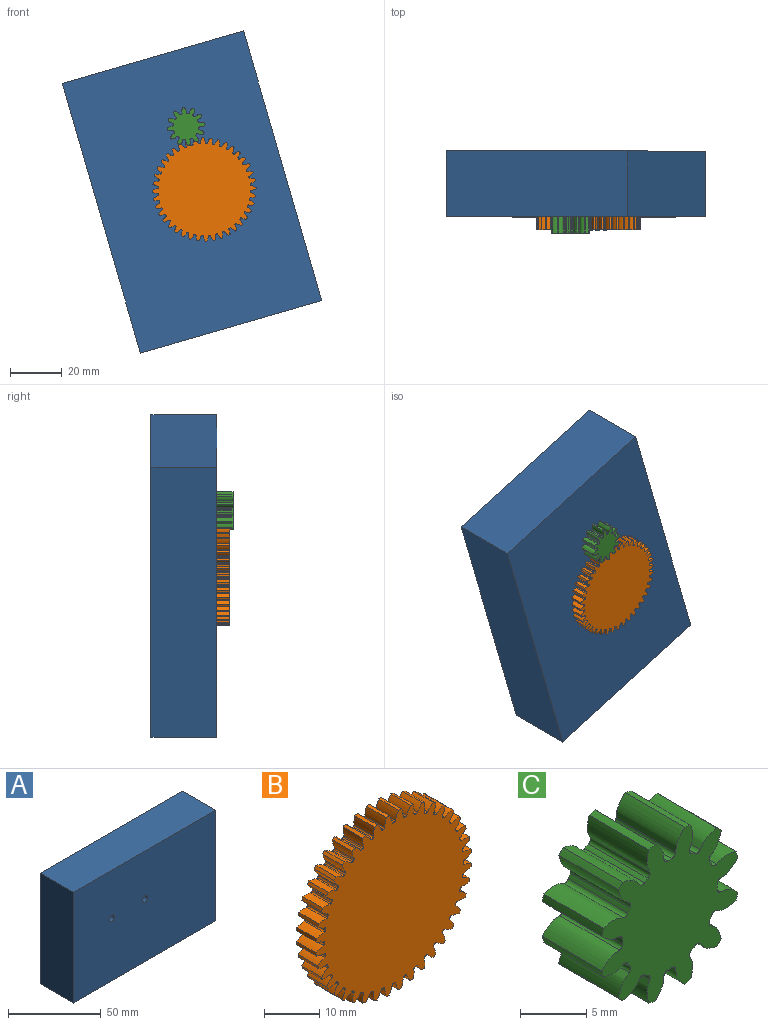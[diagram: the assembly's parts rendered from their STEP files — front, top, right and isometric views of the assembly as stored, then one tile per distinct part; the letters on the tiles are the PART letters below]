
ASSEMBLY  parts=3 mates=2
PART A: 8 faces, bbox 108.7x25.4x73 mm
  f0: plane 108.68x25.4mm, normal (0,0,1), area 2760.4mm2, adj f1,f5,f6,f7
  f1: plane 73.02x25.4mm, normal (-1,0,0), area 1854.7mm2, adj f0,f2,f6,f7
  f2: plane 108.68x25.4mm, normal (0,0,-1), area 2760.4mm2, adj f1,f5,f6,f7
  f3: cylinder r=1.91mm len=25.4mm, axis (0,-1,0), area 304mm2, adj f6,f7
  f4: cylinder r=1.91mm len=25.4mm, axis (0,-1,0), area 304mm2, adj f6,f7
  f5: plane 73.02x25.4mm, normal (1,0,0), area 1854.7mm2, adj f0,f2,f6,f7
  f6: plane 108.68x73.02mm, normal (0,1,0), area 7912.9mm2, adj f0,f1,f2,f3,f4,f5
  f7: plane 108.68x73.02mm, normal (0,-1,0), area 7912.9mm2, adj f0,f1,f2,f3,f4,f5
PART B: 242 faces, bbox 39.9x5.1x39.9 mm
  f0: extruded ~5.08x1.87mm, area 10.3mm2, adj f159,f160,f161,f162
  f1: cylinder r=17.86mm len=5.08mm, axis (0,1,0), area 1.8mm2, adj f160,f161,f162,f163
  f2: extruded ~5.08x1.87mm, area 10.3mm2, adj f3,f160,f161,f163
  f3: cylinder r=20mm len=5.08mm, axis (0,1,0), area 3.7mm2, adj f2,f4,f160,f161
  f4: extruded ~5.08x1.96mm, area 10.3mm2, adj f3,f160,f161,f164
  f5: cylinder r=17.86mm len=5.08mm, axis (0,1,0), area 1.8mm2, adj f160,f161,f164,f165
  f6: extruded ~5.08x1.73mm, area 10.3mm2, adj f7,f160,f161,f165
  f7: cylinder r=20mm len=5.08mm, axis (0,1,0), area 3.7mm2, adj f6,f8,f160,f161
  f8: extruded ~5.08x2.01mm, area 10.3mm2, adj f7,f160,f161,f166
  f9: cylinder r=17.86mm len=5.08mm, axis (0,1,0), area 1.8mm2, adj f160,f161,f166,f167
  f10: extruded ~5.08x1.55mm, area 10.3mm2, adj f11,f160,f161,f167
  f11: cylinder r=20mm len=5.08mm, axis (0,1,0), area 3.7mm2, adj f10,f12,f160,f161
  f12: extruded ~5.08x2mm, area 10.3mm2, adj f11,f160,f161,f168
  f13: cylinder r=17.86mm len=5.08mm, axis (0,1,0), area 1.8mm2, adj f160,f161,f168,f169
  f14: extruded ~5.08x1.51mm, area 10.3mm2, adj f15,f160,f161,f169
  f15: cylinder r=20mm len=5.08mm, axis (0,1,0), area 3.7mm2, adj f14,f16,f160,f161
  f16: extruded ~5.08x1.95mm, area 10.3mm2, adj f15,f160,f161,f170
  f17: cylinder r=17.86mm len=5.08mm, axis (0,1,0), area 1.8mm2, adj f160,f161,f170,f171
  f18: extruded ~5.08x1.7mm, area 10.3mm2, adj f19,f160,f161,f171
  f19: cylinder r=20mm len=5.08mm, axis (0,1,0), area 3.7mm2, adj f18,f20,f160,f161
  f20: extruded ~5.08x1.85mm, area 10.3mm2, adj f19,f160,f161,f172
  f21: cylinder r=17.86mm len=5.08mm, axis (0,1,0), area 1.8mm2, adj f160,f161,f172,f173
  f22: extruded ~5.08x1.85mm, area 10.3mm2, adj f23,f160,f161,f173
  f23: cylinder r=20mm len=5.08mm, axis (0,1,0), area 3.7mm2, adj f22,f24,f160,f161
  f24: extruded ~5.08x1.7mm, area 10.3mm2, adj f23,f160,f161,f174
  f25: cylinder r=17.86mm len=5.08mm, axis (0,1,0), area 1.8mm2, adj f160,f161,f174,f175
  f26: extruded ~5.08x1.95mm, area 10.3mm2, adj f27,f160,f161,f175
  f27: cylinder r=20mm len=5.08mm, axis (0,1,0), area 3.7mm2, adj f26,f28,f160,f161
  f28: extruded ~5.08x1.51mm, area 10.3mm2, adj f27,f160,f161,f176
  f29: cylinder r=17.86mm len=5.08mm, axis (0,1,0), area 1.8mm2, adj f160,f161,f176,f177
  f30: extruded ~5.08x2mm, area 10.3mm2, adj f31,f160,f161,f177
  f31: cylinder r=20mm len=5.08mm, axis (0,1,0), area 3.7mm2, adj f30,f32,f160,f161
  f32: extruded ~5.08x1.55mm, area 10.3mm2, adj f31,f160,f161,f178
  f33: cylinder r=17.86mm len=5.08mm, axis (0,1,0), area 1.8mm2, adj f160,f161,f178,f179
  f34: extruded ~5.08x2.01mm, area 10.3mm2, adj f35,f160,f161,f179
  f35: cylinder r=20mm len=5.08mm, axis (0,1,0), area 3.7mm2, adj f34,f36,f160,f161
  f36: extruded ~5.08x1.73mm, area 10.3mm2, adj f35,f160,f161,f180
  f37: cylinder r=17.86mm len=5.08mm, axis (0,1,0), area 1.8mm2, adj f160,f161,f180,f181
  f38: extruded ~5.08x1.96mm, area 10.3mm2, adj f39,f160,f161,f181
  f39: cylinder r=20mm len=5.08mm, axis (0,1,0), area 3.7mm2, adj f38,f40,f160,f161
  f40: extruded ~5.08x1.87mm, area 10.3mm2, adj f39,f160,f161,f182
  f41: cylinder r=17.86mm len=5.08mm, axis (0,1,0), area 1.8mm2, adj f160,f161,f182,f183
  f42: extruded ~5.08x1.87mm, area 10.3mm2, adj f43,f160,f161,f183
  f43: cylinder r=20mm len=5.08mm, axis (0,1,0), area 3.7mm2, adj f42,f44,f160,f161
  f44: extruded ~5.08x1.96mm, area 10.3mm2, adj f43,f160,f161,f184
  f45: cylinder r=17.86mm len=5.08mm, axis (0,1,0), area 1.8mm2, adj f160,f161,f184,f185
  f46: extruded ~5.08x1.73mm, area 10.3mm2, adj f47,f160,f161,f185
  f47: cylinder r=20mm len=5.08mm, axis (0,1,0), area 3.7mm2, adj f46,f48,f160,f161
  f48: extruded ~5.08x2.01mm, area 10.3mm2, adj f47,f160,f161,f186
  f49: cylinder r=17.86mm len=5.08mm, axis (0,1,0), area 1.8mm2, adj f160,f161,f186,f187
  f50: extruded ~5.08x1.55mm, area 10.3mm2, adj f51,f160,f161,f187
  f51: cylinder r=20mm len=5.08mm, axis (0,1,0), area 3.7mm2, adj f50,f52,f160,f161
  f52: extruded ~5.08x2mm, area 10.3mm2, adj f51,f160,f161,f188
  f53: cylinder r=17.86mm len=5.08mm, axis (0,1,0), area 1.8mm2, adj f160,f161,f188,f189
  f54: extruded ~5.08x1.51mm, area 10.3mm2, adj f55,f160,f161,f189
  f55: cylinder r=20mm len=5.08mm, axis (0,1,0), area 3.7mm2, adj f54,f56,f160,f161
  f56: extruded ~5.08x1.95mm, area 10.3mm2, adj f55,f160,f161,f190
  f57: cylinder r=17.86mm len=5.08mm, axis (0,1,0), area 1.8mm2, adj f160,f161,f190,f191
  f58: extruded ~5.08x1.7mm, area 10.3mm2, adj f59,f160,f161,f191
  f59: cylinder r=20mm len=5.08mm, axis (0,1,0), area 3.7mm2, adj f58,f60,f160,f161
  f60: extruded ~5.08x1.85mm, area 10.3mm2, adj f59,f160,f161,f192
  f61: cylinder r=17.86mm len=5.08mm, axis (0,1,0), area 1.8mm2, adj f160,f161,f192,f193
  f62: extruded ~5.08x1.85mm, area 10.3mm2, adj f63,f160,f161,f193
  f63: cylinder r=20mm len=5.08mm, axis (0,1,0), area 3.7mm2, adj f62,f64,f160,f161
  f64: extruded ~5.08x1.7mm, area 10.3mm2, adj f63,f160,f161,f194
  f65: cylinder r=17.86mm len=5.08mm, axis (0,1,0), area 1.8mm2, adj f160,f161,f194,f195
  f66: extruded ~5.08x1.95mm, area 10.3mm2, adj f67,f160,f161,f195
  f67: cylinder r=20mm len=5.08mm, axis (0,1,0), area 3.7mm2, adj f66,f68,f160,f161
  f68: extruded ~5.08x1.51mm, area 10.3mm2, adj f67,f160,f161,f196
  f69: cylinder r=17.86mm len=5.08mm, axis (0,1,0), area 1.8mm2, adj f160,f161,f196,f197
  f70: extruded ~5.08x2mm, area 10.3mm2, adj f71,f160,f161,f197
  f71: cylinder r=20mm len=5.08mm, axis (0,1,0), area 3.7mm2, adj f70,f72,f160,f161
  f72: extruded ~5.08x1.55mm, area 10.3mm2, adj f71,f160,f161,f198
  f73: cylinder r=17.86mm len=5.08mm, axis (0,1,0), area 1.8mm2, adj f160,f161,f198,f199
  f74: extruded ~5.08x2.01mm, area 10.3mm2, adj f75,f160,f161,f199
  f75: cylinder r=20mm len=5.08mm, axis (0,1,0), area 3.7mm2, adj f74,f76,f160,f161
  f76: extruded ~5.08x1.73mm, area 10.3mm2, adj f75,f160,f161,f200
  f77: cylinder r=17.86mm len=5.08mm, axis (0,1,0), area 1.8mm2, adj f160,f161,f200,f201
  f78: extruded ~5.08x1.96mm, area 10.3mm2, adj f79,f160,f161,f201
  f79: cylinder r=20mm len=5.08mm, axis (0,1,0), area 3.7mm2, adj f78,f80,f160,f161
  f80: extruded ~5.08x1.87mm, area 10.3mm2, adj f79,f160,f161,f202
  f81: cylinder r=17.86mm len=5.08mm, axis (0,1,0), area 1.8mm2, adj f160,f161,f202,f203
  f82: extruded ~5.08x1.87mm, area 10.3mm2, adj f83,f160,f161,f203
  f83: cylinder r=20mm len=5.08mm, axis (0,1,0), area 3.7mm2, adj f82,f84,f160,f161
  f84: extruded ~5.08x1.96mm, area 10.3mm2, adj f83,f160,f161,f204
  f85: cylinder r=17.86mm len=5.08mm, axis (0,1,0), area 1.8mm2, adj f160,f161,f204,f205
  f86: extruded ~5.08x1.73mm, area 10.3mm2, adj f87,f160,f161,f205
  f87: cylinder r=20mm len=5.08mm, axis (0,1,0), area 3.7mm2, adj f86,f88,f160,f161
  f88: extruded ~5.08x2.01mm, area 10.3mm2, adj f87,f160,f161,f206
  f89: cylinder r=17.86mm len=5.08mm, axis (0,1,0), area 1.8mm2, adj f160,f161,f206,f207
  f90: extruded ~5.08x1.55mm, area 10.3mm2, adj f91,f160,f161,f207
  f91: cylinder r=20mm len=5.08mm, axis (0,1,0), area 3.7mm2, adj f90,f92,f160,f161
  f92: extruded ~5.08x2mm, area 10.3mm2, adj f91,f160,f161,f208
  f93: cylinder r=17.86mm len=5.08mm, axis (0,1,0), area 1.8mm2, adj f160,f161,f208,f209
  f94: extruded ~5.08x1.51mm, area 10.3mm2, adj f95,f160,f161,f209
  f95: cylinder r=20mm len=5.08mm, axis (0,1,0), area 3.7mm2, adj f94,f96,f160,f161
  f96: extruded ~5.08x1.95mm, area 10.3mm2, adj f95,f160,f161,f210
  f97: cylinder r=17.86mm len=5.08mm, axis (0,1,0), area 1.8mm2, adj f160,f161,f210,f211
  f98: extruded ~5.08x1.7mm, area 10.3mm2, adj f99,f160,f161,f211
  f99: cylinder r=20mm len=5.08mm, axis (0,1,0), area 3.7mm2, adj f98,f100,f160,f161
  f100: extruded ~5.08x1.85mm, area 10.3mm2, adj f99,f160,f161,f212
  f101: cylinder r=17.86mm len=5.08mm, axis (0,1,0), area 1.8mm2, adj f160,f161,f212,f213
  f102: extruded ~5.08x1.85mm, area 10.3mm2, adj f103,f160,f161,f213
  f103: cylinder r=20mm len=5.08mm, axis (0,1,0), area 3.7mm2, adj f102,f104,f160,f161
  f104: extruded ~5.08x1.7mm, area 10.3mm2, adj f103,f160,f161,f214
  f105: cylinder r=17.86mm len=5.08mm, axis (0,1,0), area 1.8mm2, adj f160,f161,f214,f215
  f106: extruded ~5.08x1.95mm, area 10.3mm2, adj f107,f160,f161,f215
  f107: cylinder r=20mm len=5.08mm, axis (0,1,0), area 3.7mm2, adj f106,f108,f160,f161
  f108: extruded ~5.08x1.51mm, area 10.3mm2, adj f107,f160,f161,f216
  f109: cylinder r=17.86mm len=5.08mm, axis (0,1,0), area 1.8mm2, adj f160,f161,f216,f217
  f110: extruded ~5.08x2mm, area 10.3mm2, adj f111,f160,f161,f217
  f111: cylinder r=20mm len=5.08mm, axis (0,1,0), area 3.7mm2, adj f110,f112,f160,f161
  f112: extruded ~5.08x1.55mm, area 10.3mm2, adj f111,f160,f161,f218
  f113: cylinder r=17.86mm len=5.08mm, axis (0,1,0), area 1.8mm2, adj f160,f161,f218,f219
  f114: extruded ~5.08x2.01mm, area 10.3mm2, adj f115,f160,f161,f219
  f115: cylinder r=20mm len=5.08mm, axis (0,1,0), area 3.7mm2, adj f114,f116,f160,f161
  f116: extruded ~5.08x1.73mm, area 10.3mm2, adj f115,f160,f161,f220
  f117: cylinder r=17.86mm len=5.08mm, axis (0,1,0), area 1.8mm2, adj f160,f161,f220,f221
  f118: extruded ~5.08x1.96mm, area 10.3mm2, adj f119,f160,f161,f221
  f119: cylinder r=20mm len=5.08mm, axis (0,1,0), area 3.7mm2, adj f118,f120,f160,f161
  f120: extruded ~5.08x1.87mm, area 10.3mm2, adj f119,f160,f161,f222
  f121: cylinder r=17.86mm len=5.08mm, axis (0,1,0), area 1.8mm2, adj f160,f161,f222,f223
  f122: extruded ~5.08x1.87mm, area 10.3mm2, adj f123,f160,f161,f223
  f123: cylinder r=20mm len=5.08mm, axis (0,1,0), area 3.7mm2, adj f122,f124,f160,f161
  f124: extruded ~5.08x1.96mm, area 10.3mm2, adj f123,f160,f161,f224
  f125: cylinder r=17.86mm len=5.08mm, axis (0,1,0), area 1.8mm2, adj f160,f161,f224,f225
  f126: extruded ~5.08x1.73mm, area 10.3mm2, adj f127,f160,f161,f225
  f127: cylinder r=20mm len=5.08mm, axis (0,1,0), area 3.7mm2, adj f126,f128,f160,f161
  f128: extruded ~5.08x2.01mm, area 10.3mm2, adj f127,f160,f161,f226
  f129: cylinder r=17.86mm len=5.08mm, axis (0,1,0), area 1.8mm2, adj f160,f161,f226,f227
  f130: extruded ~5.08x1.55mm, area 10.3mm2, adj f131,f160,f161,f227
  f131: cylinder r=20mm len=5.08mm, axis (0,1,0), area 3.7mm2, adj f130,f132,f160,f161
  f132: extruded ~5.08x2mm, area 10.3mm2, adj f131,f160,f161,f228
  f133: cylinder r=17.86mm len=5.08mm, axis (0,1,0), area 1.8mm2, adj f160,f161,f228,f229
  f134: extruded ~5.08x1.51mm, area 10.3mm2, adj f135,f160,f161,f229
  f135: cylinder r=20mm len=5.08mm, axis (0,1,0), area 3.7mm2, adj f134,f136,f160,f161
  f136: extruded ~5.08x1.95mm, area 10.3mm2, adj f135,f160,f161,f230
  f137: cylinder r=17.86mm len=5.08mm, axis (0,1,0), area 1.8mm2, adj f160,f161,f230,f231
  f138: extruded ~5.08x1.7mm, area 10.3mm2, adj f139,f160,f161,f231
  f139: cylinder r=20mm len=5.08mm, axis (0,1,0), area 3.7mm2, adj f138,f140,f160,f161
  f140: extruded ~5.08x1.85mm, area 10.3mm2, adj f139,f160,f161,f232
  f141: cylinder r=17.86mm len=5.08mm, axis (0,1,0), area 1.8mm2, adj f160,f161,f232,f233
  f142: extruded ~5.08x1.85mm, area 10.3mm2, adj f143,f160,f161,f233
  f143: cylinder r=20mm len=5.08mm, axis (0,1,0), area 3.7mm2, adj f142,f144,f160,f161
  f144: extruded ~5.08x1.7mm, area 10.3mm2, adj f143,f160,f161,f234
  f145: cylinder r=17.86mm len=5.08mm, axis (0,1,0), area 1.8mm2, adj f160,f161,f234,f235
  f146: extruded ~5.08x1.95mm, area 10.3mm2, adj f147,f160,f161,f235
  f147: cylinder r=20mm len=5.08mm, axis (0,1,0), area 3.7mm2, adj f146,f148,f160,f161
  f148: extruded ~5.08x1.51mm, area 10.3mm2, adj f147,f160,f161,f236
  f149: cylinder r=17.86mm len=5.08mm, axis (0,1,0), area 1.8mm2, adj f160,f161,f236,f237
  f150: extruded ~5.08x2mm, area 10.3mm2, adj f151,f160,f161,f237
  f151: cylinder r=20mm len=5.08mm, axis (0,1,0), area 3.7mm2, adj f150,f152,f160,f161
  f152: extruded ~5.08x1.55mm, area 10.3mm2, adj f151,f160,f161,f238
  f153: cylinder r=17.86mm len=5.08mm, axis (0,1,0), area 1.8mm2, adj f160,f161,f238,f239
  f154: extruded ~5.08x2.01mm, area 10.3mm2, adj f155,f160,f161,f239
  f155: cylinder r=20mm len=5.08mm, axis (0,1,0), area 3.7mm2, adj f154,f156,f160,f161
  f156: extruded ~5.08x1.73mm, area 10.3mm2, adj f155,f160,f161,f240
  f157: cylinder r=17.86mm len=5.08mm, axis (0,1,0), area 1.8mm2, adj f160,f161,f240,f241
  f158: extruded ~5.08x1.96mm, area 10.3mm2, adj f159,f160,f161,f241
  f159: cylinder r=20mm len=5.08mm, axis (0,1,0), area 3.7mm2, adj f0,f158,f160,f161
  f160: plane 39.93x39.93mm, normal (0,-1,0), area 1131.2mm2, adj f0,f1,f2,f3,f4,f5,f6,f7
  f161: plane 39.93x39.93mm, normal (0,1,0), area 1131.2mm2, adj f0,f1,f2,f3,f4,f5,f6,f7
  f162: cylinder r=0.29mm len=5.08mm, axis (0,1,0), area 2.1mm2, adj f0,f1,f160,f161
  f163: cylinder r=0.29mm len=5.08mm, axis (0,1,0), area 2.1mm2, adj f1,f2,f160,f161
  f164: cylinder r=0.29mm len=5.08mm, axis (0,1,0), area 2.1mm2, adj f4,f5,f160,f161
  f165: cylinder r=0.29mm len=5.08mm, axis (0,1,0), area 2.1mm2, adj f5,f6,f160,f161
  f166: cylinder r=0.29mm len=5.08mm, axis (0,1,0), area 2.1mm2, adj f8,f9,f160,f161
  f167: cylinder r=0.29mm len=5.08mm, axis (0,1,0), area 2.1mm2, adj f9,f10,f160,f161
  f168: cylinder r=0.29mm len=5.08mm, axis (0,1,0), area 2.1mm2, adj f12,f13,f160,f161
  f169: cylinder r=0.29mm len=5.08mm, axis (0,1,0), area 2.1mm2, adj f13,f14,f160,f161
  f170: cylinder r=0.29mm len=5.08mm, axis (0,1,0), area 2.1mm2, adj f16,f17,f160,f161
  f171: cylinder r=0.29mm len=5.08mm, axis (0,1,0), area 2.1mm2, adj f17,f18,f160,f161
  f172: cylinder r=0.29mm len=5.08mm, axis (0,1,0), area 2.1mm2, adj f20,f21,f160,f161
  f173: cylinder r=0.29mm len=5.08mm, axis (0,1,0), area 2.1mm2, adj f21,f22,f160,f161
  f174: cylinder r=0.29mm len=5.08mm, axis (0,1,0), area 2.1mm2, adj f24,f25,f160,f161
  f175: cylinder r=0.29mm len=5.08mm, axis (0,1,0), area 2.1mm2, adj f25,f26,f160,f161
  f176: cylinder r=0.29mm len=5.08mm, axis (0,1,0), area 2.1mm2, adj f28,f29,f160,f161
  f177: cylinder r=0.29mm len=5.08mm, axis (0,1,0), area 2.1mm2, adj f29,f30,f160,f161
  f178: cylinder r=0.29mm len=5.08mm, axis (0,1,0), area 2.1mm2, adj f32,f33,f160,f161
  f179: cylinder r=0.29mm len=5.08mm, axis (0,1,0), area 2.1mm2, adj f33,f34,f160,f161
  f180: cylinder r=0.29mm len=5.08mm, axis (0,1,0), area 2.1mm2, adj f36,f37,f160,f161
  f181: cylinder r=0.29mm len=5.08mm, axis (0,1,0), area 2.1mm2, adj f37,f38,f160,f161
  f182: cylinder r=0.29mm len=5.08mm, axis (0,1,0), area 2.1mm2, adj f40,f41,f160,f161
  f183: cylinder r=0.29mm len=5.08mm, axis (0,1,0), area 2.1mm2, adj f41,f42,f160,f161
  f184: cylinder r=0.29mm len=5.08mm, axis (0,1,0), area 2.1mm2, adj f44,f45,f160,f161
  f185: cylinder r=0.29mm len=5.08mm, axis (0,1,0), area 2.1mm2, adj f45,f46,f160,f161
  f186: cylinder r=0.29mm len=5.08mm, axis (0,1,0), area 2.1mm2, adj f48,f49,f160,f161
  f187: cylinder r=0.29mm len=5.08mm, axis (0,1,0), area 2.1mm2, adj f49,f50,f160,f161
  f188: cylinder r=0.29mm len=5.08mm, axis (0,1,0), area 2.1mm2, adj f52,f53,f160,f161
  f189: cylinder r=0.29mm len=5.08mm, axis (0,1,0), area 2.1mm2, adj f53,f54,f160,f161
  f190: cylinder r=0.29mm len=5.08mm, axis (0,1,0), area 2.1mm2, adj f56,f57,f160,f161
  f191: cylinder r=0.29mm len=5.08mm, axis (0,1,0), area 2.1mm2, adj f57,f58,f160,f161
  f192: cylinder r=0.29mm len=5.08mm, axis (0,1,0), area 2.1mm2, adj f60,f61,f160,f161
  f193: cylinder r=0.29mm len=5.08mm, axis (0,1,0), area 2.1mm2, adj f61,f62,f160,f161
  f194: cylinder r=0.29mm len=5.08mm, axis (0,1,0), area 2.1mm2, adj f64,f65,f160,f161
  f195: cylinder r=0.29mm len=5.08mm, axis (0,1,0), area 2.1mm2, adj f65,f66,f160,f161
  f196: cylinder r=0.29mm len=5.08mm, axis (0,1,0), area 2.1mm2, adj f68,f69,f160,f161
  f197: cylinder r=0.29mm len=5.08mm, axis (0,1,0), area 2.1mm2, adj f69,f70,f160,f161
  f198: cylinder r=0.29mm len=5.08mm, axis (0,1,0), area 2.1mm2, adj f72,f73,f160,f161
  f199: cylinder r=0.29mm len=5.08mm, axis (0,1,0), area 2.1mm2, adj f73,f74,f160,f161
  f200: cylinder r=0.29mm len=5.08mm, axis (0,1,0), area 2.1mm2, adj f76,f77,f160,f161
  f201: cylinder r=0.29mm len=5.08mm, axis (0,1,0), area 2.1mm2, adj f77,f78,f160,f161
  f202: cylinder r=0.29mm len=5.08mm, axis (0,1,0), area 2.1mm2, adj f80,f81,f160,f161
  f203: cylinder r=0.29mm len=5.08mm, axis (0,1,0), area 2.1mm2, adj f81,f82,f160,f161
  f204: cylinder r=0.29mm len=5.08mm, axis (0,1,0), area 2.1mm2, adj f84,f85,f160,f161
  f205: cylinder r=0.29mm len=5.08mm, axis (0,1,0), area 2.1mm2, adj f85,f86,f160,f161
  f206: cylinder r=0.29mm len=5.08mm, axis (0,1,0), area 2.1mm2, adj f88,f89,f160,f161
  f207: cylinder r=0.29mm len=5.08mm, axis (0,1,0), area 2.1mm2, adj f89,f90,f160,f161
  f208: cylinder r=0.29mm len=5.08mm, axis (0,1,0), area 2.1mm2, adj f92,f93,f160,f161
  f209: cylinder r=0.29mm len=5.08mm, axis (0,1,0), area 2.1mm2, adj f93,f94,f160,f161
  f210: cylinder r=0.29mm len=5.08mm, axis (0,1,0), area 2.1mm2, adj f96,f97,f160,f161
  f211: cylinder r=0.29mm len=5.08mm, axis (0,1,0), area 2.1mm2, adj f97,f98,f160,f161
  f212: cylinder r=0.29mm len=5.08mm, axis (0,1,0), area 2.1mm2, adj f100,f101,f160,f161
  f213: cylinder r=0.29mm len=5.08mm, axis (0,1,0), area 2.1mm2, adj f101,f102,f160,f161
  f214: cylinder r=0.29mm len=5.08mm, axis (0,1,0), area 2.1mm2, adj f104,f105,f160,f161
  f215: cylinder r=0.29mm len=5.08mm, axis (0,1,0), area 2.1mm2, adj f105,f106,f160,f161
  f216: cylinder r=0.29mm len=5.08mm, axis (0,1,0), area 2.1mm2, adj f108,f109,f160,f161
  f217: cylinder r=0.29mm len=5.08mm, axis (0,1,0), area 2.1mm2, adj f109,f110,f160,f161
  f218: cylinder r=0.29mm len=5.08mm, axis (0,1,0), area 2.1mm2, adj f112,f113,f160,f161
  f219: cylinder r=0.29mm len=5.08mm, axis (0,1,0), area 2.1mm2, adj f113,f114,f160,f161
  f220: cylinder r=0.29mm len=5.08mm, axis (0,1,0), area 2.1mm2, adj f116,f117,f160,f161
  f221: cylinder r=0.29mm len=5.08mm, axis (0,1,0), area 2.1mm2, adj f117,f118,f160,f161
  f222: cylinder r=0.29mm len=5.08mm, axis (0,1,0), area 2.1mm2, adj f120,f121,f160,f161
  f223: cylinder r=0.29mm len=5.08mm, axis (0,1,0), area 2.1mm2, adj f121,f122,f160,f161
  f224: cylinder r=0.29mm len=5.08mm, axis (0,1,0), area 2.1mm2, adj f124,f125,f160,f161
  f225: cylinder r=0.29mm len=5.08mm, axis (0,1,0), area 2.1mm2, adj f125,f126,f160,f161
  f226: cylinder r=0.29mm len=5.08mm, axis (0,1,0), area 2.1mm2, adj f128,f129,f160,f161
  f227: cylinder r=0.29mm len=5.08mm, axis (0,1,0), area 2.1mm2, adj f129,f130,f160,f161
  f228: cylinder r=0.29mm len=5.08mm, axis (0,1,0), area 2.1mm2, adj f132,f133,f160,f161
  f229: cylinder r=0.29mm len=5.08mm, axis (0,1,0), area 2.1mm2, adj f133,f134,f160,f161
  f230: cylinder r=0.29mm len=5.08mm, axis (0,1,0), area 2.1mm2, adj f136,f137,f160,f161
  f231: cylinder r=0.29mm len=5.08mm, axis (0,1,0), area 2.1mm2, adj f137,f138,f160,f161
  f232: cylinder r=0.29mm len=5.08mm, axis (0,1,0), area 2.1mm2, adj f140,f141,f160,f161
  f233: cylinder r=0.29mm len=5.08mm, axis (0,1,0), area 2.1mm2, adj f141,f142,f160,f161
  f234: cylinder r=0.29mm len=5.08mm, axis (0,1,0), area 2.1mm2, adj f144,f145,f160,f161
  f235: cylinder r=0.29mm len=5.08mm, axis (0,1,0), area 2.1mm2, adj f145,f146,f160,f161
  f236: cylinder r=0.29mm len=5.08mm, axis (0,1,0), area 2.1mm2, adj f148,f149,f160,f161
  f237: cylinder r=0.29mm len=5.08mm, axis (0,1,0), area 2.1mm2, adj f149,f150,f160,f161
  f238: cylinder r=0.29mm len=5.08mm, axis (0,1,0), area 2.1mm2, adj f152,f153,f160,f161
  f239: cylinder r=0.29mm len=5.08mm, axis (0,1,0), area 2.1mm2, adj f153,f154,f160,f161
  f240: cylinder r=0.29mm len=5.08mm, axis (0,1,0), area 2.1mm2, adj f156,f157,f160,f161
  f241: cylinder r=0.29mm len=5.08mm, axis (0,1,0), area 2.1mm2, adj f157,f158,f160,f161
PART C: 74 faces, bbox 14.5x6.4x14.5 mm
  f0: extruded ~6.35x1.87mm, area 13.8mm2, adj f47,f48,f49,f50
  f1: cylinder r=5.03mm len=6.35mm, axis (0,1,0), area 2.8mm2, adj f48,f49,f50,f51
  f2: extruded ~6.35x1.87mm, area 13.8mm2, adj f3,f48,f49,f51
  f3: cylinder r=7.41mm len=6.35mm, axis (0,1,0), area 4.2mm2, adj f2,f4,f48,f49
  f4: extruded ~6.35x2.11mm, area 13.8mm2, adj f3,f48,f49,f52
  f5: cylinder r=5.03mm len=6.35mm, axis (0,1,0), area 2.8mm2, adj f48,f49,f52,f53
  f6: extruded ~6.35x1.78mm, area 13.8mm2, adj f7,f48,f49,f53
  f7: cylinder r=7.41mm len=6.35mm, axis (0,1,0), area 4.2mm2, adj f6,f8,f48,f49
  f8: extruded ~6.35x1.78mm, area 13.8mm2, adj f7,f48,f49,f54
  f9: cylinder r=5.03mm len=6.35mm, axis (0,1,0), area 2.8mm2, adj f48,f49,f54,f55
  f10: extruded ~6.35x2.11mm, area 13.8mm2, adj f11,f48,f49,f55
  f11: cylinder r=7.41mm len=6.35mm, axis (0,1,0), area 4.2mm2, adj f10,f12,f48,f49
  f12: extruded ~6.35x1.87mm, area 13.8mm2, adj f11,f48,f49,f56
  f13: cylinder r=5.03mm len=6.35mm, axis (0,1,0), area 2.8mm2, adj f48,f49,f56,f57
  f14: extruded ~6.35x1.87mm, area 13.8mm2, adj f15,f48,f49,f57
  f15: cylinder r=7.41mm len=6.35mm, axis (0,1,0), area 4.2mm2, adj f14,f16,f48,f49
  f16: extruded ~6.35x2.11mm, area 13.8mm2, adj f15,f48,f49,f58
  f17: cylinder r=5.03mm len=6.35mm, axis (0,1,0), area 2.8mm2, adj f48,f49,f58,f59
  f18: extruded ~6.35x1.78mm, area 13.8mm2, adj f19,f48,f49,f59
  f19: cylinder r=7.41mm len=6.35mm, axis (0,1,0), area 4.2mm2, adj f18,f20,f48,f49
  f20: extruded ~6.35x1.78mm, area 13.8mm2, adj f19,f48,f49,f60
  f21: cylinder r=5.03mm len=6.35mm, axis (0,1,0), area 2.8mm2, adj f48,f49,f60,f61
  f22: extruded ~6.35x2.11mm, area 13.8mm2, adj f23,f48,f49,f61
  f23: cylinder r=7.41mm len=6.35mm, axis (0,1,0), area 4.2mm2, adj f22,f24,f48,f49
  f24: extruded ~6.35x1.87mm, area 13.8mm2, adj f23,f48,f49,f62
  f25: cylinder r=5.03mm len=6.35mm, axis (0,1,0), area 2.8mm2, adj f48,f49,f62,f63
  f26: extruded ~6.35x1.87mm, area 13.8mm2, adj f27,f48,f49,f63
  f27: cylinder r=7.41mm len=6.35mm, axis (0,1,0), area 4.2mm2, adj f26,f28,f48,f49
  f28: extruded ~6.35x2.11mm, area 13.8mm2, adj f27,f48,f49,f64
  f29: cylinder r=5.03mm len=6.35mm, axis (0,1,0), area 2.8mm2, adj f48,f49,f64,f65
  f30: extruded ~6.35x1.78mm, area 13.8mm2, adj f31,f48,f49,f65
  f31: cylinder r=7.41mm len=6.35mm, axis (0,1,0), area 4.2mm2, adj f30,f32,f48,f49
  f32: extruded ~6.35x1.78mm, area 13.8mm2, adj f31,f48,f49,f66
  f33: cylinder r=5.03mm len=6.35mm, axis (0,1,0), area 2.8mm2, adj f48,f49,f66,f67
  f34: extruded ~6.35x2.11mm, area 13.8mm2, adj f35,f48,f49,f67
  f35: cylinder r=7.41mm len=6.35mm, axis (0,1,0), area 4.2mm2, adj f34,f36,f48,f49
  f36: extruded ~6.35x1.87mm, area 13.8mm2, adj f35,f48,f49,f68
  f37: cylinder r=5.03mm len=6.35mm, axis (0,1,0), area 2.8mm2, adj f48,f49,f68,f69
  f38: extruded ~6.35x1.87mm, area 13.8mm2, adj f39,f48,f49,f69
  f39: cylinder r=7.41mm len=6.35mm, axis (0,1,0), area 4.2mm2, adj f38,f40,f48,f49
  f40: extruded ~6.35x2.11mm, area 13.8mm2, adj f39,f48,f49,f70
  f41: cylinder r=5.03mm len=6.35mm, axis (0,1,0), area 2.8mm2, adj f48,f49,f70,f71
  f42: extruded ~6.35x1.78mm, area 13.8mm2, adj f43,f48,f49,f71
  f43: cylinder r=7.41mm len=6.35mm, axis (0,1,0), area 4.2mm2, adj f42,f44,f48,f49
  f44: extruded ~6.35x1.78mm, area 13.8mm2, adj f43,f48,f49,f72
  f45: cylinder r=5.03mm len=6.35mm, axis (0,1,0), area 2.8mm2, adj f48,f49,f72,f73
  f46: extruded ~6.35x2.11mm, area 13.8mm2, adj f47,f48,f49,f73
  f47: cylinder r=7.41mm len=6.35mm, axis (0,1,0), area 4.2mm2, adj f0,f46,f48,f49
  f48: plane 14.51x14.51mm, normal (0,-1,0), area 121.8mm2, adj f0,f1,f2,f3,f4,f5,f6,f7
  f49: plane 14.51x14.51mm, normal (0,1,0), area 121.8mm2, adj f0,f1,f2,f3,f4,f5,f6,f7
  f50: cylinder r=0.39mm len=6.35mm, axis (0,1,0), area 3.7mm2, adj f0,f1,f48,f49
  f51: cylinder r=0.39mm len=6.35mm, axis (0,1,0), area 3.7mm2, adj f1,f2,f48,f49
  f52: cylinder r=0.39mm len=6.35mm, axis (0,1,0), area 3.7mm2, adj f4,f5,f48,f49
  f53: cylinder r=0.39mm len=6.35mm, axis (0,1,0), area 3.7mm2, adj f5,f6,f48,f49
  f54: cylinder r=0.39mm len=6.35mm, axis (0,1,0), area 3.7mm2, adj f8,f9,f48,f49
  f55: cylinder r=0.39mm len=6.35mm, axis (0,1,0), area 3.7mm2, adj f9,f10,f48,f49
  f56: cylinder r=0.39mm len=6.35mm, axis (0,1,0), area 3.7mm2, adj f12,f13,f48,f49
  f57: cylinder r=0.39mm len=6.35mm, axis (0,1,0), area 3.7mm2, adj f13,f14,f48,f49
  f58: cylinder r=0.39mm len=6.35mm, axis (0,1,0), area 3.7mm2, adj f16,f17,f48,f49
  f59: cylinder r=0.39mm len=6.35mm, axis (0,1,0), area 3.7mm2, adj f17,f18,f48,f49
  f60: cylinder r=0.39mm len=6.35mm, axis (0,1,0), area 3.7mm2, adj f20,f21,f48,f49
  f61: cylinder r=0.39mm len=6.35mm, axis (0,1,0), area 3.7mm2, adj f21,f22,f48,f49
  f62: cylinder r=0.39mm len=6.35mm, axis (0,1,0), area 3.7mm2, adj f24,f25,f48,f49
  f63: cylinder r=0.39mm len=6.35mm, axis (0,1,0), area 3.7mm2, adj f25,f26,f48,f49
  f64: cylinder r=0.39mm len=6.35mm, axis (0,1,0), area 3.7mm2, adj f28,f29,f48,f49
  f65: cylinder r=0.39mm len=6.35mm, axis (0,1,0), area 3.7mm2, adj f29,f30,f48,f49
  f66: cylinder r=0.39mm len=6.35mm, axis (0,1,0), area 3.7mm2, adj f32,f33,f48,f49
  f67: cylinder r=0.39mm len=6.35mm, axis (0,1,0), area 3.7mm2, adj f33,f34,f48,f49
  f68: cylinder r=0.39mm len=6.35mm, axis (0,1,0), area 3.7mm2, adj f36,f37,f48,f49
  f69: cylinder r=0.39mm len=6.35mm, axis (0,1,0), area 3.7mm2, adj f37,f38,f48,f49
  f70: cylinder r=0.39mm len=6.35mm, axis (0,1,0), area 3.7mm2, adj f40,f41,f48,f49
  f71: cylinder r=0.39mm len=6.35mm, axis (0,1,0), area 3.7mm2, adj f41,f42,f48,f49
  f72: cylinder r=0.39mm len=6.35mm, axis (0,1,0), area 3.7mm2, adj f44,f45,f48,f49
  f73: cylinder r=0.39mm len=6.35mm, axis (0,1,0), area 3.7mm2, adj f45,f46,f48,f49
PLACE A rot(axis=(0,1,0),73.8deg) t=(-120.08,-3.55,-31.08)mm fixed
PLACE B rot(axis=(0,-1,0),159.3deg) t=(-115.06,-3.55,-26.15)mm
PLACE C rot(axis=(0,-1,0),53deg) t=(-122.13,-3.55,-1.76)mm
MATE revolute A.f3 <-> C.f3  axis (0,-1,0) through (-122.13,-3.55,-1.76)mm
MATE revolute A.f4 <-> B.f3  axis (0,-1,0) through (-115.06,-3.55,-26.15)mm
